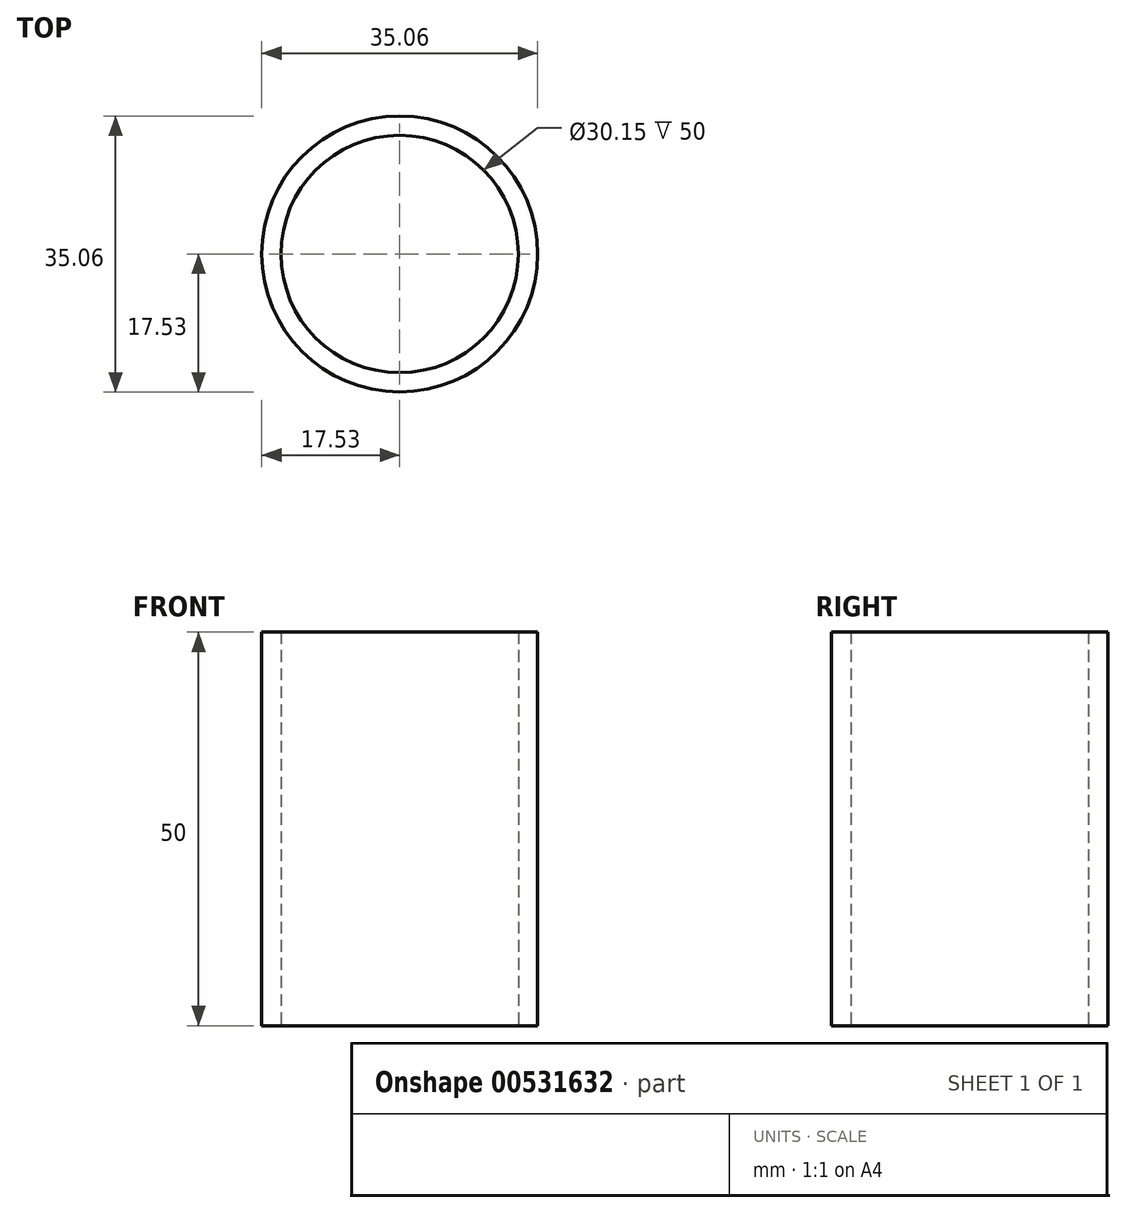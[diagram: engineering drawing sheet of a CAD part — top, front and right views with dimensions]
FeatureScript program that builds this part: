
annotation { "Feature Type Name" : "Feature", "Feature Type Description" : "" }
export const myFeature = defineFeature(function(context is Context, id is Id, definition is map)
    precondition{}
    {
        {
            var Q0;
            Q0=qCreatedBy(makeId("Top.planeOp"),FACE);
            var sketch = newSketch(context, id + "F0", { "sketchPlane" : qUnion([Q0])});
            skCircle(sketch, "E0", {"center": v(0, 0) * mm, "radius": 17.53 * mm});
            skCircle(sketch, "E1", {"center": v(0, 0) * mm, "radius": 15.08 * mm});
            skSolve(sketch);
        }
        {
            var Q0;
            Q0 = qSketchRegion(id + "F0", true);
            extrude(context, id + "F1", {"entities" : qUnion([Q0]), "depth" : 50 * mm, "offsetDistance" : 25 * mm});
        }
    });
